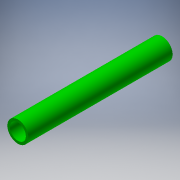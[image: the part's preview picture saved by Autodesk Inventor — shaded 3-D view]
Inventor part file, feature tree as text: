
AUTODESK INVENTOR PART (.ipt)
format: ipt  version: 2018.2 (Build 222227000, 227)  size: 109,056 bytes
history: native  units: in
note: dims shown in document units (in); Inventor stores cm internally (conversion verified against a paired STEP export)
features: extrude x1, sketch x1
ambient origin geometry x8: Origin, YZ Plane, XZ Plane, XY Plane, X Axis, Y Axis, Z Axis, Center Point
bodies: Solid1 (feature_tree)
feature tree (2):
  extrude  "Extrusion1"  Depth=9.0in
  sketch  "Sketch1"  dims[d0=1.315in d1=1.0in d2=9.0in d3=0.0in]
